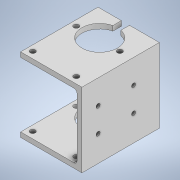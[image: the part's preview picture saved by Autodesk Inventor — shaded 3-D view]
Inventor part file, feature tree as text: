
AUTODESK INVENTOR PART (.ipt)
format: ipt  version: 2022 (Build 260153000, 153)  size: 194,048 bytes
history: native  units: mm
features: sketch x7, extrude x3, hole x3, other x1, fillet x1
ambient origin geometry x8: Origin, YZ Plane, XZ Plane, XY Plane, X Axis, Y Axis, Z Axis, Center Point
bodies: Body1 (feature_tree)
feature tree (15):
  other  "ソリッド1"
  extrude  "押し出し1"  Depth=48.0mm
  extrude  "押し出し2"  Depth=38.0mm
  hole  "穴1"  [1 undecoded]
  hole  "穴2"  [1 undecoded]
  sketch  "スケッチ6"
  fillet  "フィレット1"  Radius=3.0mm
  hole  "穴5"  [1 undecoded]
  extrude  "押し出し4"  Depth=100.0mm TaperAngle=0.0deg
  sketch  "スケッチ1"
  sketch  "スケッチ2"
  sketch  "スケッチ3"
  sketch  "スケッチ4"
  sketch  "スケッチ8"
  sketch  "スケッチ9"
note: 3 required parameter values undecoded (feature->parameter linkage not recoverable at this tier; creation-order binding heuristic only, values carry confidence <= 0.55)
